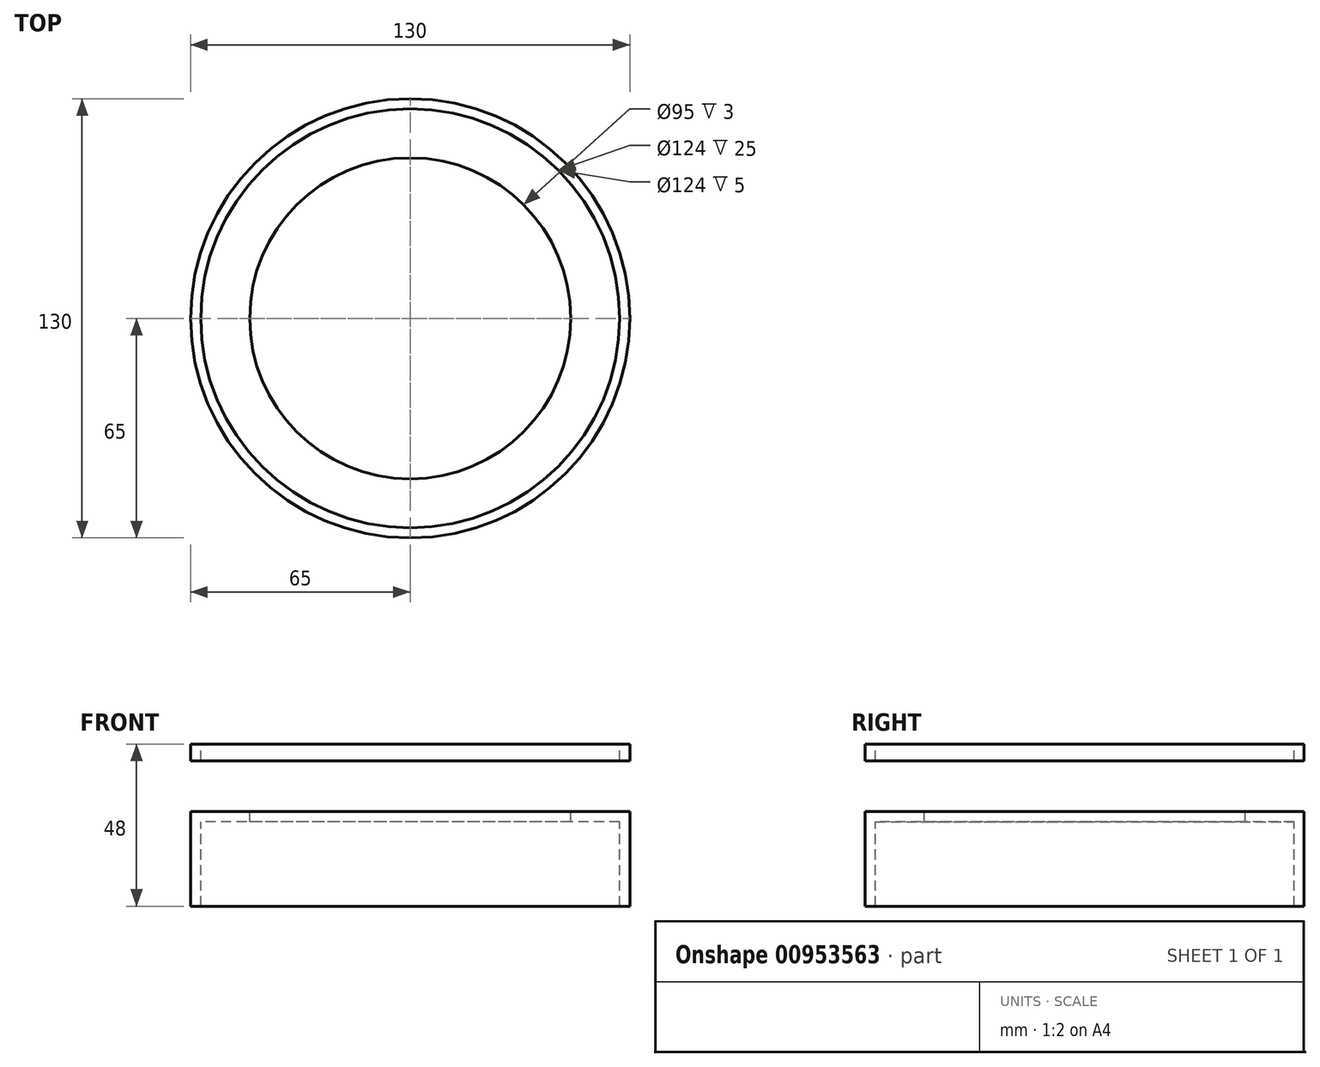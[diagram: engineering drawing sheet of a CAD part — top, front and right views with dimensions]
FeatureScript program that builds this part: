
annotation { "Feature Type Name" : "Feature", "Feature Type Description" : "" }
export const myFeature = defineFeature(function(context is Context, id is Id, definition is map)
    precondition{}
    {
        {
            var Q0;
            Q0=qCreatedBy(makeId("Front.planeOp"),FACE);
            var sketch = newSketch(context, id + "F0", { "sketchPlane" : qUnion([Q0])});
            skLineSegment(sketch, "E0", {"start": v(47.5, 28) * mm, "end": v(47.5, 25) * mm});
            skLineSegment(sketch, "E1", {"start": v(62, 0) * mm, "end": v(65, 0) * mm});
            skLineSegment(sketch, "E2", {"start": v(0, 70.32) * mm, "end": v(0, -47.87) * mm, "construction": true});
            skLineSegment(sketch, "E3", {"start": v(47.5, 25) * mm, "end": v(62, 25) * mm});
            skLineSegment(sketch, "E4", {"start": v(62, 25) * mm, "end": v(62, 0) * mm});
            skLineSegment(sketch, "E5", {"start": v(65, 0) * mm, "end": v(65, 28) * mm});
            skLineSegment(sketch, "E6", {"start": v(65, 28) * mm, "end": v(47.5, 28) * mm});
            skPoint(sketch, "E7", {"position": v(65, 43) * mm});
            skLineSegment(sketch, "E8.bottom", {"start": v(65, 43) * mm, "end": v(62, 43) * mm});
            skLineSegment(sketch, "E8.top", {"start": v(65, 48) * mm, "end": v(62, 48) * mm});
            skLineSegment(sketch, "E8.left", {"start": v(65, 43) * mm, "end": v(65, 48) * mm});
            skLineSegment(sketch, "E8.right", {"start": v(62, 43) * mm, "end": v(62, 48) * mm});
            skSolve(sketch);
        }
        {
            var Q0;
            Q0=qSketchRegion(id+"F0",true);
            var Q1;
            Q1=sQuery(id+"F0.wireOp",EDGE,"E2");
            revolve(context, id + "F1", {"surfaceOperationType" : NewSurfaceOperationType.NEW, "entities" : qUnion([Q0]), "axis" : qUnion([Q1]), "revolveType" : RevolveType.FULL});
        }
    });
